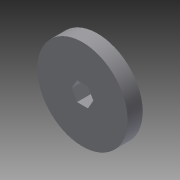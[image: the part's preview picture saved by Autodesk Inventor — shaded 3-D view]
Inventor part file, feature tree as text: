
AUTODESK INVENTOR PART (.ipt)
format: ipt  version: 2014 SP1 (Build 180222100, 222)  size: 81,408 bytes
history: native  units: in
note: dims shown in document units (in); Inventor stores cm internally (conversion verified against a paired STEP export)
features: extrude x1, sketch x1
ambient origin geometry x8: Origin, YZ Plane, XZ Plane, XY Plane, X Axis, Y Axis, Z Axis, Center Point
bodies: Solid1 (feature_tree)
feature tree (2):
  extrude  "Extrusion1"  Depth=0.5in
  sketch  "Sketch1"  dims[d0=2.4in d1=0.5in d2=0.4in d3=0.0in]
